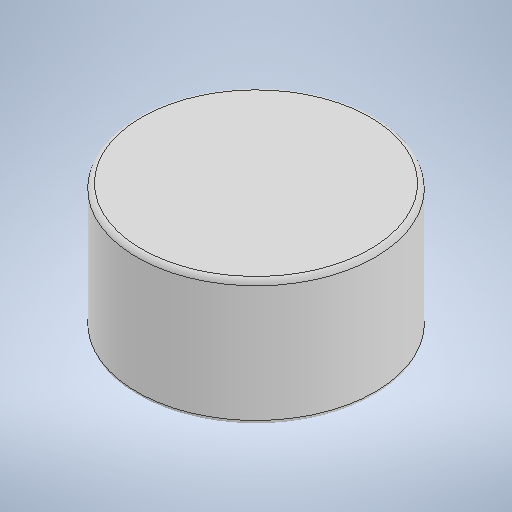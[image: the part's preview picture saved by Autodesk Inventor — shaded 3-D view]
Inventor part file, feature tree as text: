
AUTODESK INVENTOR PART (.ipt)
format: ipt  version: 2025 (Build 290162000, 162)  size: 214,016 bytes
history: native  units: mm
features: extrude x1, fillet x1, sketch x1
ambient origin geometry x8: Origin, YZ Plane, XZ Plane, XY Plane, X Axis, Y Axis, Z Axis, Center Point
bodies: Solid1 (feature_tree)
feature tree (3):
  extrude  "Extrusion1"  Depth=2.65mm TaperAngle=0.0deg
  fillet  "Fillet1"  Radius=0.1mm
  sketch  "Sketch1"  dims[d0=5.0mm d1=2.65mm d2=0.0mm d3=0.1mm]
